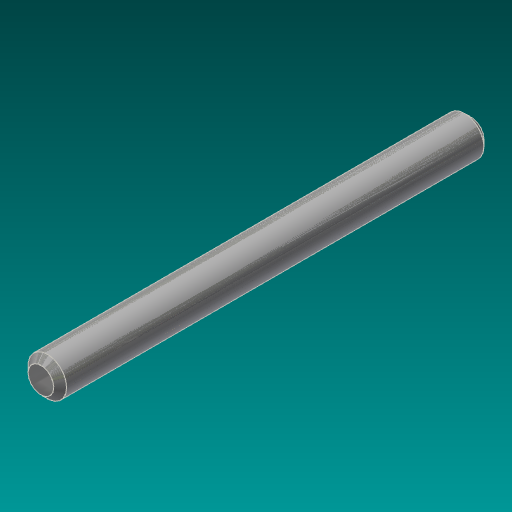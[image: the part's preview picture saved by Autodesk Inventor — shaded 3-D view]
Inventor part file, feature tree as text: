
AUTODESK INVENTOR PART (.ipt)
format: ipt  version: 2017.3 (Build 213256000, 256)  size: 113,664 bytes
history: native  units: in
note: dims shown in document units (in); Inventor stores cm internally (conversion verified against a paired STEP export)
features: extrude x1, chamfer x1, sketch x1
ambient origin geometry x8: Origin, YZ Plane, XZ Plane, XY Plane, X Axis, Y Axis, Z Axis, Center Point
bodies: Solid1 (feature_tree)
feature tree (3):
  extrude  "Extrusion1"  Depth=4.1875in TaperAngle=0.0deg
  chamfer  "Chamfer1"  Distance=0.0625in Angle=45.0deg
  sketch  "Sketch1"  dims[d0=0.375in d1=4.1875in d2=0.0in d3=0.0625in d4=0.125in d5=45.0deg]
